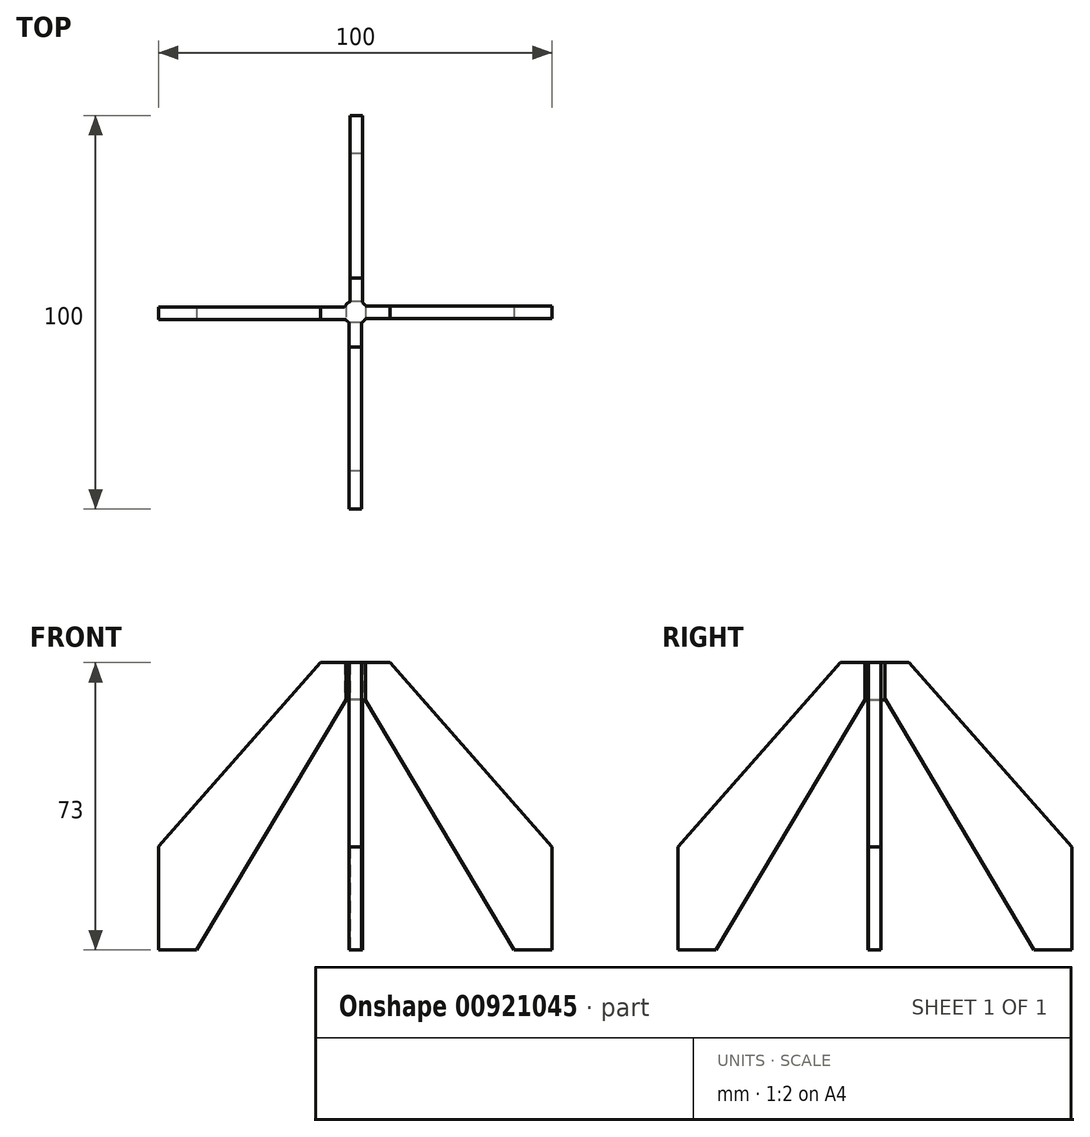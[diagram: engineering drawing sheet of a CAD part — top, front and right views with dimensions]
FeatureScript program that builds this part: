
annotation { "Feature Type Name" : "Feature", "Feature Type Description" : "" }
export const myFeature = defineFeature(function(context is Context, id is Id, definition is map)
    precondition{}
    {
        {
            var Q0;
            Q0=qCreatedBy(makeId("Top.planeOp"),FACE);
            var sketch = newSketch(context, id + "F0", { "sketchPlane" : qUnion([Q0])});
            skCircle(sketch, "E0", {"center": v(0, 0) * mm, "radius": 3.05 * mm});
            skSolve(sketch);
        }
        {
            var Q0;
            Q0=makeQuery(id+"F0.imprint","IMPRINT",FACE,{"disambiguationData":[TD([[makeQuery(id+"F0.imprint","IMPRINT",EDGE,{"derivedFrom":sQuery(id+"F0.wireOp",EDGE,"E0")}),1.0]])]});
            extrude(context, id + "F1", {"entities" : qUnion([Q0]), "depth" : 110 * mm, "offsetDistance" : 25.4 * mm});
        }
        {
            var Q0;
            Q0=qCreatedBy(makeId("Top.planeOp"),FACE);
            var sketch = newSketch(context, id + "F2", { "sketchPlane" : qUnion([Q0])});
            skLineSegment(sketch, "E1.bottom", {"start": v(1.6, 0) * mm, "end": v(-1.58, 0) * mm});
            skLineSegment(sketch, "E1.top", {"start": v(1.6, -50) * mm, "end": v(-1.58, -50) * mm});
            skLineSegment(sketch, "E1.left", {"start": v(1.6, 0) * mm, "end": v(1.6, -50) * mm});
            skLineSegment(sketch, "E1.right", {"start": v(-1.58, 0) * mm, "end": v(-1.58, -50) * mm});
            skSolve(sketch);
        }
        {
            var Q0;
            Q0=makeQuery(id+"F2.imprint","IMPRINT",FACE,{"disambiguationData":[TD([[makeQuery(id+"F2.imprint","IMPRINT",EDGE,{"derivedFrom":sQuery(id+"F2.wireOp",EDGE,"E1.bottom")}),1.0]])]});
            extrude(context, id + "F3", {"entities" : qUnion([Q0]), "operationType" : NewBodyOperationType.ADD, "depth" : 80 * mm, "offsetDistance" : 25.4 * mm});
        }
        {
            var Q0;
            Q0=makeQuery(id+"F3.opExtrude","SWEPT_FACE",FACE,{"disambiguationData":[OSD([sQuery(id+"F2.wireOp",EDGE,"E1.right")])]});
            var sketch = newSketch(context, id + "F4", { "sketchPlane" : qUnion([Q0])});
            skLineSegment(sketch, "E2", {"start": v(2.6, 80) * mm, "end": v(50, 26.2) * mm});
            skSolve(sketch);
        }
        {
            var Q0;
            {var subQ0=sQuery(id+"F4.wireOp",EDGE,"E2");Q0=makeQuery(id+"F4.imprint","IMPRINT",FACE,{"disambiguationData":[TD([[makeQuery(id+"F4.imprint","IMPRINT",EDGE,{"derivedFrom":subQ0}),1.0]])]});}
            extrude(context, id + "F5", {"entities" : qUnion([Q0]), "operationType" : NewBodyOperationType.REMOVE, "endBound" : BoundingType.UP_TO_NEXT, "oppositeDirection" : true, "depth" : 25.4 * mm, "offsetDistance" : 25.4 * mm});
        }
        {
            var Q0;
            Q0=qCreatedBy(makeId("Top.planeOp"),FACE);
            var sketch = newSketch(context, id + "F6", { "sketchPlane" : qUnion([Q0])});
            skLineSegment(sketch, "E3.bottom", {"start": v(0, 1.57) * mm, "end": v(50, 1.57) * mm});
            skLineSegment(sketch, "E3.top", {"start": v(0, -1.6) * mm, "end": v(50, -1.6) * mm});
            skLineSegment(sketch, "E3.left", {"start": v(0, 1.57) * mm, "end": v(0, -1.6) * mm});
            skLineSegment(sketch, "E3.right", {"start": v(50, 1.57) * mm, "end": v(50, -1.6) * mm});
            skSolve(sketch);
        }
        {
            var Q0;
            Q0=makeQuery(id+"F6.imprint","IMPRINT",FACE,{"disambiguationData":[TD([[makeQuery(id+"F6.imprint","IMPRINT",EDGE,{"derivedFrom":sQuery(id+"F6.wireOp",EDGE,"E3.bottom")}),-1.0]])]});
            extrude(context, id + "F7", {"entities" : qUnion([Q0]), "operationType" : NewBodyOperationType.ADD, "depth" : 80 * mm, "offsetDistance" : 25.4 * mm});
        }
        {
            var Q0;
            Q0=makeQuery(id+"F7.opExtrude","SWEPT_FACE",FACE,{"disambiguationData":[OSD([sQuery(id+"F6.wireOp",EDGE,"E3.top")])]});
            var sketch = newSketch(context, id + "F8", { "sketchPlane" : qUnion([Q0])});
            skLineSegment(sketch, "E4", {"start": v(2.59, 80) * mm, "end": v(2.59, 26.17) * mm});
            skLineSegment(sketch, "E5", {"start": v(2.59, 26.17) * mm, "end": v(50, 26.17) * mm});
            skLineSegment(sketch, "E6", {"start": v(50, 26.17) * mm, "end": v(2.59, 80) * mm});
            skSolve(sketch);
        }
        {
            var Q0;
            {var subQ0=sQuery(id+"F8.wireOp",EDGE,"E6");Q0=makeQuery(id+"F8.imprint","IMPRINT",FACE,{"disambiguationData":[TD([[makeQuery(id+"F8.imprint","IMPRINT",EDGE,{"derivedFrom":subQ0}),-1.0]])]});}
            extrude(context, id + "F9", {"entities" : qUnion([Q0]), "operationType" : NewBodyOperationType.REMOVE, "endBound" : BoundingType.UP_TO_NEXT, "oppositeDirection" : true, "depth" : 25.4 * mm, "offsetDistance" : 25.4 * mm});
        }
        {
            var Q0;
            Q0=qCreatedBy(makeId("Top.planeOp"),FACE);
            var sketch = newSketch(context, id + "F10", { "sketchPlane" : qUnion([Q0])});
            skLineSegment(sketch, "E7.bottom", {"start": v(1.78, 0) * mm, "end": v(-1.4, 0) * mm});
            skLineSegment(sketch, "E7.top", {"start": v(1.78, 50) * mm, "end": v(-1.4, 50) * mm});
            skLineSegment(sketch, "E7.left", {"start": v(1.78, 0) * mm, "end": v(1.78, 50) * mm});
            skLineSegment(sketch, "E7.right", {"start": v(-1.4, 0) * mm, "end": v(-1.4, 50) * mm});
            skSolve(sketch);
        }
        {
            var Q0;
            Q0=makeQuery(id+"F10.imprint","IMPRINT",FACE,{"disambiguationData":[TD([[makeQuery(id+"F10.imprint","IMPRINT",EDGE,{"derivedFrom":sQuery(id+"F10.wireOp",EDGE,"E7.bottom")}),-1.0]])]});
            extrude(context, id + "F11", {"entities" : qUnion([Q0]), "operationType" : NewBodyOperationType.ADD, "depth" : 80 * mm, "offsetDistance" : 25.4 * mm});
        }
        {
            var Q0;
            Q0=makeQuery(id+"F11.opExtrude","SWEPT_FACE",FACE,{"disambiguationData":[OSD([sQuery(id+"F10.wireOp",EDGE,"E7.left")])]});
            var sketch = newSketch(context, id + "F12", { "sketchPlane" : qUnion([Q0])});
            skLineSegment(sketch, "E8", {"start": v(2.48, 80) * mm, "end": v(2.48, 26.2) * mm});
            skLineSegment(sketch, "E9", {"start": v(2.48, 26.2) * mm, "end": v(50, 26.2) * mm});
            skLineSegment(sketch, "E10", {"start": v(50, 26.2) * mm, "end": v(2.48, 80) * mm});
            skSolve(sketch);
        }
        {
            var Q0;
            {var subQ0=sQuery(id+"F12.wireOp",EDGE,"E10");Q0=makeQuery(id+"F12.imprint","IMPRINT",FACE,{"disambiguationData":[TD([[makeQuery(id+"F12.imprint","IMPRINT",EDGE,{"derivedFrom":subQ0}),-1.0]])]});}
            extrude(context, id + "F13", {"entities" : qUnion([Q0]), "operationType" : NewBodyOperationType.REMOVE, "endBound" : BoundingType.UP_TO_NEXT, "oppositeDirection" : true, "depth" : 25.4 * mm, "offsetDistance" : 25.4 * mm});
        }
        {
            var Q0;
            Q0=qCreatedBy(makeId("Top.planeOp"),FACE);
            var sketch = newSketch(context, id + "F14", { "sketchPlane" : qUnion([Q0])});
            skLineSegment(sketch, "E11.bottom", {"start": v(0, -1.84) * mm, "end": v(-50, -1.84) * mm});
            skLineSegment(sketch, "E11.top", {"start": v(0, 1.34) * mm, "end": v(-50, 1.34) * mm});
            skLineSegment(sketch, "E11.left", {"start": v(0, -1.84) * mm, "end": v(0, 1.34) * mm});
            skLineSegment(sketch, "E11.right", {"start": v(-50, -1.84) * mm, "end": v(-50, 1.34) * mm});
            skSolve(sketch);
        }
        {
            var Q0;
            Q0=makeQuery(id+"F14.imprint","IMPRINT",FACE,{"disambiguationData":[TD([[makeQuery(id+"F14.imprint","IMPRINT",EDGE,{"derivedFrom":sQuery(id+"F14.wireOp",EDGE,"E11.bottom")}),-1.0]])]});
            extrude(context, id + "F15", {"entities" : qUnion([Q0]), "operationType" : NewBodyOperationType.ADD, "depth" : 80 * mm, "offsetDistance" : 25.4 * mm});
        }
        {
            var Q0;
            Q0=makeQuery(id+"F15.opExtrude","SWEPT_FACE",FACE,{"disambiguationData":[OSD([sQuery(id+"F14.wireOp",EDGE,"E11.top")])]});
            var sketch = newSketch(context, id + "F16", { "sketchPlane" : qUnion([Q0])});
            skLineSegment(sketch, "E12", {"start": v(2.74, 80) * mm, "end": v(2.74, 26.27) * mm});
            skLineSegment(sketch, "E13", {"start": v(2.74, 26.27) * mm, "end": v(50, 26.27) * mm});
            skLineSegment(sketch, "E14", {"start": v(50, 26.27) * mm, "end": v(2.74, 80) * mm});
            skSolve(sketch);
        }
        {
            var Q0;
            {var subQ0=sQuery(id+"F16.wireOp",EDGE,"E14");Q0=makeQuery(id+"F16.imprint","IMPRINT",FACE,{"disambiguationData":[TD([[makeQuery(id+"F16.imprint","IMPRINT",EDGE,{"derivedFrom":subQ0}),-1.0]])]});}
            extrude(context, id + "F17", {"entities" : qUnion([Q0]), "operationType" : NewBodyOperationType.REMOVE, "endBound" : BoundingType.UP_TO_NEXT, "oppositeDirection" : true, "depth" : 25.4 * mm, "offsetDistance" : 25.4 * mm});
        }
        {
            var Q0;
            Q0=makeQuery(id+"F1.opExtrude","CAP_FACE",FACE,{"disambiguationData":[OSD([sQuery(id+"F0.wireOp",EDGE,"E0")])],"isStart":false});
            var sketch = newSketch(context, id + "F18", { "sketchPlane" : qUnion([Q0])});
            skCircle(sketch, "E15", {"center": v(0, 0) * mm, "radius": 5.3 * mm});
            skSolve(sketch);
        }
        {
            var Q0;
            Q0 = qSketchRegion(id + "F18", true);
            extrude(context, id + "F19", {"entities" : qUnion([Q0]), "operationType" : NewBodyOperationType.ADD, "depth" : 5 * mm, "offsetDistance" : 25.4 * mm});
        }
        {
            var Q0;
            Q0=makeQuery(id+"F19.opExtrude","CAP_FACE",FACE,{"disambiguationData":[OSD([sQuery(id+"F18.wireOp",EDGE,"E15")])],"isStart":false});
            var sketch = newSketch(context, id + "F20", { "sketchPlane" : qUnion([Q0])});
            skSolve(sketch);
        }
        {
            var Q0;
            Q0=makeQuery(id+"F19.opExtrude","CAP_EDGE",EDGE,{"disambiguationData":[OSD([sQuery(id+"F18.wireOp",EDGE,"E15")])],"isStart":true});
            fillet(context, id + "F21", {"entities" : qUnion([Q0]), "radius" : 5.08 * mm, "tangentPropagation" : true, "allowEdgeOverflow" : false});
        }
        {
            var Q0;
            Q0=makeQuery(id+"F20.imprint","IMPRINT",FACE,{"disambiguationData":[TD([[makeQuery(id+"F20.imprint","IMPRINT",EDGE,{"derivedFrom":makeQuery(id+"F19.opExtrude","CAP_EDGE",EDGE,{"disambiguationData":[OSD([sQuery(id+"F18.wireOp",EDGE,"E15")])],"isStart":false})}),1.0]])]});
            var sketch = newSketch(context, id + "F22", { "sketchPlane" : qUnion([Q0])});
            skCircle(sketch, "E16", {"center": v(0, 0) * mm, "radius": 9.43 * mm});
            skSolve(sketch);
        }
        {
            var Q0;
            Q0=makeQuery(id+"F22.imprint","IMPRINT",FACE,{"disambiguationData":[TD([[makeQuery(id+"F22.imprint","IMPRINT",EDGE,{"derivedFrom":sQuery(id+"F22.wireOp",EDGE,"E16")}),1.0]])]});
            var Q1;
            Q1=makeQuery(id+"F20.imprint","IMPRINT",FACE,{"disambiguationData":[TD([[makeQuery(id+"F20.imprint","IMPRINT",EDGE,{"derivedFrom":makeQuery(id+"F19.opExtrude","CAP_EDGE",EDGE,{"disambiguationData":[OSD([sQuery(id+"F18.wireOp",EDGE,"E15")])],"isStart":false})}),1.0]])]});
            extrude(context, id + "F23", {"entities" : qUnion([Q0, Q1]), "operationType" : NewBodyOperationType.REMOVE, "oppositeDirection" : true, "depth" : 42 * mm, "offsetDistance" : 25.4 * mm});
        }
        {
            var Q0;
            Q0=makeQuery(id+"F7.opExtrude","SWEPT_FACE",FACE,{"disambiguationData":[OSD([sQuery(id+"F6.wireOp",EDGE,"E3.top")])]});
            var sketch = newSketch(context, id + "F24", { "sketchPlane" : qUnion([Q0])});
            skLineSegment(sketch, "E17", {"start": v(2.59, 0) * mm, "end": v(2.59, 51.3) * mm});
            skLineSegment(sketch, "E18", {"start": v(2.59, 63.43) * mm, "end": v(40.35, 0) * mm});
            skLineSegment(sketch, "E19", {"start": v(50, 0) * mm, "end": v(40.35, 0) * mm, "construction": true});
            skSolve(sketch);
        }
        {
            var Q0;
            {var subQ0=sQuery(id+"F24.wireOp",EDGE,"E17");Q0=makeQuery(id+"F24.imprint","IMPRINT",FACE,{"disambiguationData":[TD([[makeQuery(id+"F24.imprint","IMPRINT",EDGE,{"derivedFrom":subQ0}),1.0]])]});}
            extrude(context, id + "F25", {"entities" : qUnion([Q0]), "operationType" : NewBodyOperationType.REMOVE, "endBound" : BoundingType.UP_TO_NEXT, "oppositeDirection" : true, "depth" : 25.4 * mm, "offsetDistance" : 25.4 * mm});
        }
        {
            var Q0;
            Q0=makeQuery(id+"F15.opExtrude","SWEPT_FACE",FACE,{"disambiguationData":[OSD([sQuery(id+"F14.wireOp",EDGE,"E11.bottom")])]});
            var sketch = newSketch(context, id + "F26", { "sketchPlane" : qUnion([Q0])});
            skLineSegment(sketch, "E20", {"start": v(-50, 13.13) * mm, "end": v(-40.34, 13.13) * mm, "construction": true});
            skLineSegment(sketch, "E21", {"start": v(-40.34, 0) * mm, "end": v(-2.43, 63.57) * mm});
            skSolve(sketch);
        }
        {
            var Q0;
            {var subQ0=sQuery(id+"F26.wireOp",EDGE,"E21");Q0=makeQuery(id+"F26.imprint","IMPRINT",FACE,{"disambiguationData":[TD([[makeQuery(id+"F26.imprint","IMPRINT",EDGE,{"derivedFrom":subQ0}),-1.0]])]});}
            extrude(context, id + "F27", {"entities" : qUnion([Q0]), "operationType" : NewBodyOperationType.REMOVE, "endBound" : BoundingType.UP_TO_NEXT, "oppositeDirection" : true, "depth" : 25.4 * mm, "offsetDistance" : 25.4 * mm});
        }
        {
            var Q0;
            Q0=makeQuery(id+"F3.opExtrude","SWEPT_FACE",FACE,{"disambiguationData":[OSD([sQuery(id+"F2.wireOp",EDGE,"E1.right")])]});
            var sketch = newSketch(context, id + "F28", { "sketchPlane" : qUnion([Q0])});
            skLineSegment(sketch, "E22", {"start": v(50, 9.83) * mm, "end": v(40.35, 9.83) * mm, "construction": true});
            skLineSegment(sketch, "E23", {"start": v(40.35, 0) * mm, "end": v(2.6, 63.53) * mm});
            skSolve(sketch);
        }
        {
            var Q0;
            {var subQ0=sQuery(id+"F28.wireOp",EDGE,"E23");Q0=makeQuery(id+"F28.imprint","IMPRINT",FACE,{"disambiguationData":[TD([[makeQuery(id+"F28.imprint","IMPRINT",EDGE,{"derivedFrom":subQ0}),1.0]])]});}
            extrude(context, id + "F29", {"entities" : qUnion([Q0]), "operationType" : NewBodyOperationType.REMOVE, "endBound" : BoundingType.UP_TO_NEXT, "oppositeDirection" : true, "depth" : 25.4 * mm, "offsetDistance" : 25.4 * mm});
        }
        {
            var Q0;
            Q0=makeQuery(id+"F11.opExtrude","SWEPT_FACE",FACE,{"disambiguationData":[OSD([sQuery(id+"F10.wireOp",EDGE,"E7.right")])]});
            var sketch = newSketch(context, id + "F30", { "sketchPlane" : qUnion([Q0])});
            skLineSegment(sketch, "E24", {"start": v(-50, 7.52) * mm, "end": v(-40.35, 7.52) * mm, "construction": true});
            skLineSegment(sketch, "E25", {"start": v(-40.35, 0) * mm, "end": v(-2.7, 63.7) * mm});
            skSolve(sketch);
        }
        {
            var Q0;
            {var subQ0=sQuery(id+"F30.wireOp",EDGE,"E25");Q0=makeQuery(id+"F30.imprint","IMPRINT",FACE,{"disambiguationData":[TD([[makeQuery(id+"F30.imprint","IMPRINT",EDGE,{"derivedFrom":subQ0}),-1.0]])]});}
            extrude(context, id + "F31", {"entities" : qUnion([Q0]), "operationType" : NewBodyOperationType.REMOVE, "endBound" : BoundingType.UP_TO_NEXT, "oppositeDirection" : true, "depth" : 25.4 * mm, "offsetDistance" : 25.4 * mm});
        }
        {
            var Q0;
            {var subQ0=sQuery(id+"F6.wireOp",EDGE,"E3.top");var subQ1=sQuery(id+"F0.wireOp",EDGE,"E0");var subQ4=sQuery(id+"F2.wireOp",EDGE,"E1.right");var subQ6=sQuery(id+"F2.wireOp",EDGE,"E1.left");var subQ8=sQuery(id+"F10.wireOp",EDGE,"E7.left");var subQ10=makeQuery(id+"F1.opExtrude","SWEPT_FACE",FACE,{"disambiguationData":[OSD([subQ1])]});var subQ11=sQuery(id+"F14.wireOp",EDGE,"E11.bottom");var subQ14=sQuery(id+"F10.wireOp",EDGE,"E7.right");var subQ15=sQuery(id+"F10.wireOp",EDGE,"E7.top");var subQ19=sQuery(id+"F2.wireOp",EDGE,"E1.top");var subQ21=sQuery(id+"F14.wireOp",EDGE,"E11.top");var subQ22=sQuery(id+"F14.wireOp",EDGE,"E11.right");Q0=makeQuery(id+"F31.boolean.opBoolean","SPLIT",FACE,{"disambiguationData":[TD([subQ10])],"derivedFrom":makeQuery(id+"F29.boolean.opBoolean","SPLIT",FACE,{"disambiguationData":[TD([subQ10])],"derivedFrom":makeQuery(id+"F27.boolean.opBoolean","SPLIT",FACE,{"disambiguationData":[TD([subQ10])],"derivedFrom":makeQuery(id+"F25.boolean.opBoolean","SPLIT",FACE,{"disambiguationData":[TD([subQ10])],"derivedFrom":makeQuery(id+"F15.boolean.opBoolean","MERGE",FACE,{"derivedFrom":[makeQuery(id+"F11.boolean.opBoolean","MERGE",FACE,{"derivedFrom":[makeQuery(id+"F7.boolean.opBoolean","MERGE",FACE,{"derivedFrom":[makeQuery(id+"F3.boolean.opBoolean","MERGE",FACE,{"derivedFrom":[makeQuery(id+"F1.opExtrude","CAP_FACE",FACE,{"disambiguationData":[OSD([subQ1])],"isStart":true}),makeQuery(id+"F3.opExtrude","CAP_FACE",FACE,{"disambiguationData":[OSD([sQuery(id+"F2.wireOp",EDGE,"E1.bottom"),subQ19,subQ6,subQ4])],"isStart":true})]}),makeQuery(id+"F7.opExtrude","CAP_FACE",FACE,{"disambiguationData":[OSD([sQuery(id+"F6.wireOp",EDGE,"E3.bottom"),subQ0,sQuery(id+"F6.wireOp",EDGE,"E3.left"),sQuery(id+"F6.wireOp",EDGE,"E3.right")])],"isStart":true})]}),makeQuery(id+"F11.opExtrude","CAP_FACE",FACE,{"disambiguationData":[OSD([sQuery(id+"F10.wireOp",EDGE,"E7.bottom"),subQ15,subQ8,subQ14])],"isStart":true})]}),makeQuery(id+"F15.opExtrude","CAP_FACE",FACE,{"disambiguationData":[OSD([subQ11,subQ21,sQuery(id+"F14.wireOp",EDGE,"E11.left"),subQ22])],"isStart":true})]})})})})});}
            extrude(context, id + "F32", {"entities" : qUnion([Q0]), "operationType" : NewBodyOperationType.REMOVE, "oppositeDirection" : true, "depth" : 63.5 * mm, "offsetDistance" : 25.4 * mm});
        }
    });
